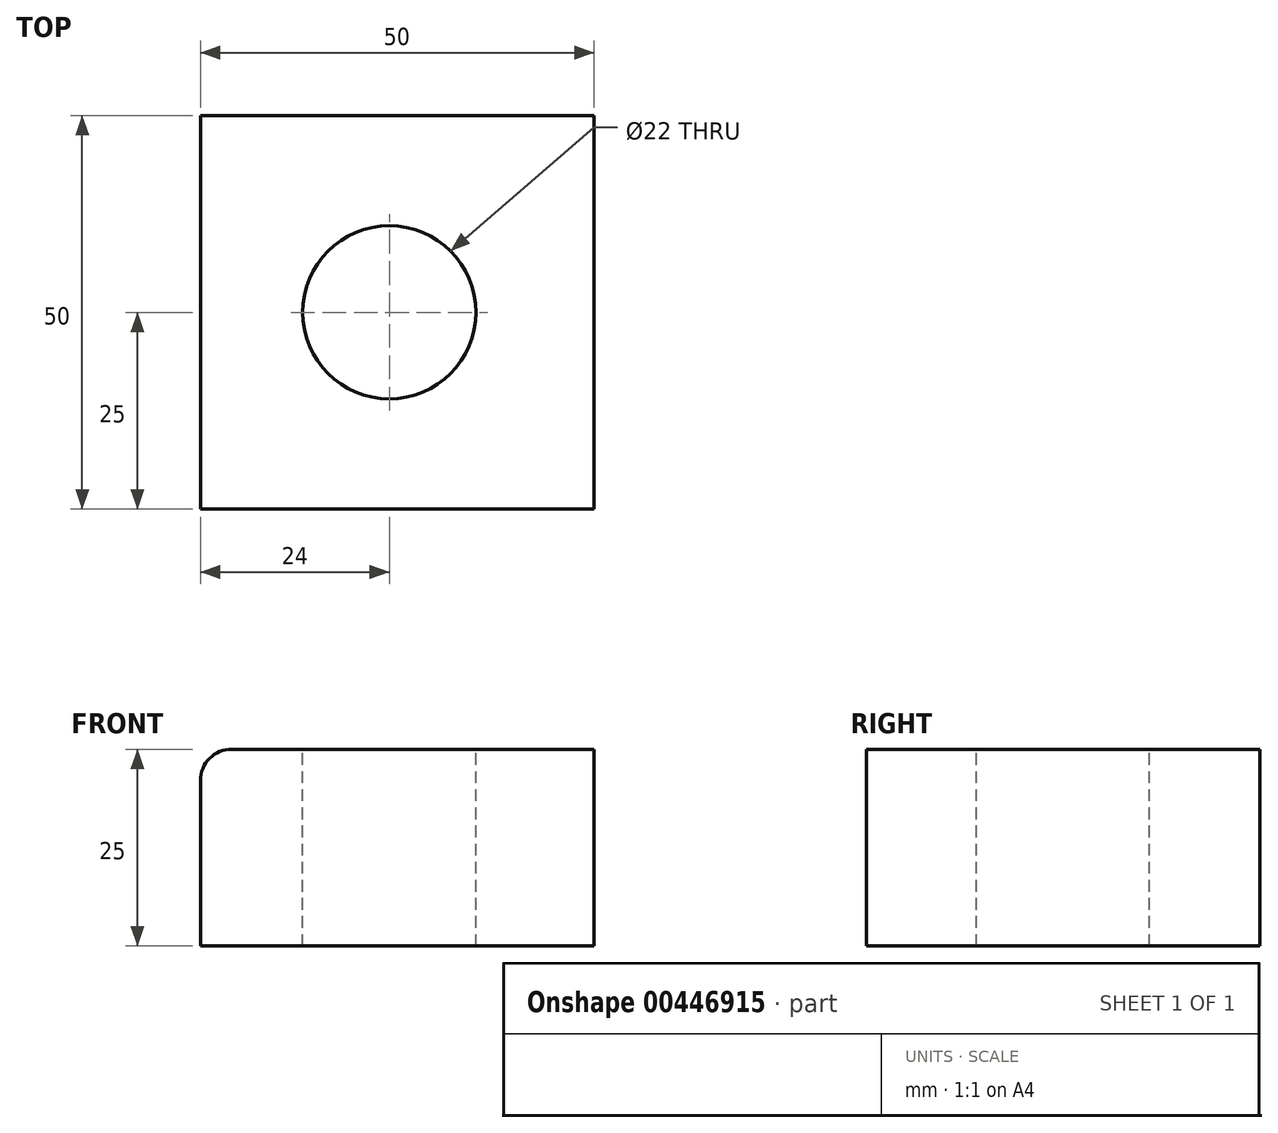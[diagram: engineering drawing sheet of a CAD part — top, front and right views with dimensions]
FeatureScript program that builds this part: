
annotation { "Feature Type Name" : "Feature", "Feature Type Description" : "" }
export const myFeature = defineFeature(function(context is Context, id is Id, definition is map)
    precondition{}
    {
        {
            var Q0;
            Q0=qCreatedBy(makeId("Front.planeOp"),FACE);
            var sketch = newSketch(context, id + "F0", { "sketchPlane" : qUnion([Q0])});
            skLineSegment(sketch, "E0", {"start": v(26, 0) * mm, "end": v(-24, 0) * mm});
            skLineSegment(sketch, "E1", {"start": v(-24, 0) * mm, "end": v(-24, -25) * mm});
            skLineSegment(sketch, "E2", {"start": v(-24, -25) * mm, "end": v(26, -25) * mm});
            skLineSegment(sketch, "E3", {"start": v(26, -25) * mm, "end": v(26, 0) * mm});
            skSolve(sketch);
        }
        {
            var Q0;
            Q0=qSketchRegion(id+"F0",true);
            extrude(context, id + "F1", {"entities" : qUnion([Q0]), "endBound" : BoundingType.SYMMETRIC, "depth" : 50 * mm});
        }
        {
            var Q0;
            Q0=makeQuery(id+"F1.opExtrude","SWEPT_EDGE",EDGE,{"disambiguationData":[OSD([sQuery(id+"F0.wireOp",EDGE,"E0"),sQuery(id+"F0.wireOp",EDGE,"E1")])]});
            fillet(context, id + "F2", {"entities" : qUnion([Q0]), "radius" : 4 * mm, "tangentPropagation" : true, "allowEdgeOverflow" : false});
        }
        {
            var Q0;
            Q0=makeQuery(id+"F1.opExtrude","SWEPT_FACE",FACE,{"disambiguationData":[OSD([sQuery(id+"F0.wireOp",EDGE,"E0")])]});
            var sketch = newSketch(context, id + "F3", { "sketchPlane" : qUnion([Q0])});
            skCircle(sketch, "E4", {"center": v(0, 0) * mm, "radius": 11 * mm});
            skSolve(sketch);
        }
        {
            var Q0;
            Q0=qSketchRegion(id+"F3",true);
            extrude(context, id + "F4", {"entities" : qUnion([Q0]), "operationType" : NewBodyOperationType.REMOVE, "endBound" : BoundingType.THROUGH_ALL, "oppositeDirection" : true, "depth" : 25 * mm});
        }
    });
